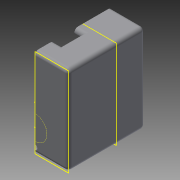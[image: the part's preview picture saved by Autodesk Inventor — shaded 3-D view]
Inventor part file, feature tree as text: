
AUTODESK INVENTOR PART (.ipt)
format: ipt  version: 2013 (Build 170138000, 138)  size: 355,840 bytes
history: native  units: mm
features: sketch x13, extrude x11, fillet x5, plane x1, other x1
ambient origin geometry x8: Origin, YZ Plane, XZ Plane, XY Plane, X Axis, Y Axis, Z Axis, Center Point
bodies: Solid1 (feature_tree)
feature tree (31):
  extrude  "Extrusion1"  Depth=47.5mm
  extrude  "Extrusion2"  Depth=12.2mm
  sketch  "Sketch3"  dims[d6=16.67mm d7=0.0mm d8=14.85mm]
  extrude  "Extrusion3"  Depth=14.85mm
  extrude  "Extrusion4"  Depth=13.0mm
  sketch  "Sketch6"  dims[d17=2.0mm d18=3.0mm d19=0.0mm]
  extrude  "Extrusion5"  Depth=3.0mm
  plane  "Work Plane1"
  extrude  "Extrusion6"  Depth=3.0mm TaperAngle=0.0deg
  extrude  "Extrusion7"  Depth=4.0mm TaperAngle=0.0deg
  sketch  "Sketch13"  dims[d28=5.0mm d29=12.5mm d30=0.0mm]
  extrude  "Extrusion8"  Depth=6.5mm
  extrude  "Extrusion9"  Depth=15.0mm
  extrude  "Extrusion10"  Depth=12.5mm TaperAngle=0.0deg
  extrude  "Extrusion11"  Depth=1.5mm TaperAngle=0.0deg
  fillet  "Fillet1"  Radius=3.0mm
  fillet  "Fillet2"  Radius=20.0mm
  fillet  "Fillet3"  Radius=4.0mm
  fillet  "Fillet4"  Radius=11.0mm
  fillet  "Fillet5"  Radius=4.0mm
  sketch  "Sketch1"  dims[d0=18.0mm d1=47.5mm]
  sketch  "Sketch2"  dims[d2=25.67mm d3=0.0mm d4=12.2mm]
  sketch  "Sketch4"  dims[d10=22.67mm d11=0.0mm d12=13.0mm]
  sketch  "Sketch5"  dims[d13=6.0mm d14=0.0mm d15=3.0mm]
  sketch  "Sketch7"  dims[d20=45.0deg d21=4.0mm d22=0.0mm]
  sketch  "Sketch11"  dims[d23=5.0mm d24=6.5mm]
  sketch  "Sketch12"  dims[d25=20.0mm d26=0.0mm d27=15.0mm]
  sketch  "Sketch14"  dims[d32=0.5mm d35=1.5mm d36=0.0mm d37=3.0mm d38=0.0mm d39=20.0mm d40=4.0mm d41=11.0mm d42=4.0mm d43=0.0mm]
  other  "Pin Trench"
  sketch  "Sketch16"  dims[d44=2.0mm]
  sketch  "Sketch17"  dims[d45=0.5mm d46=0.5mm d47=0.5mm d48=2.0mm]
